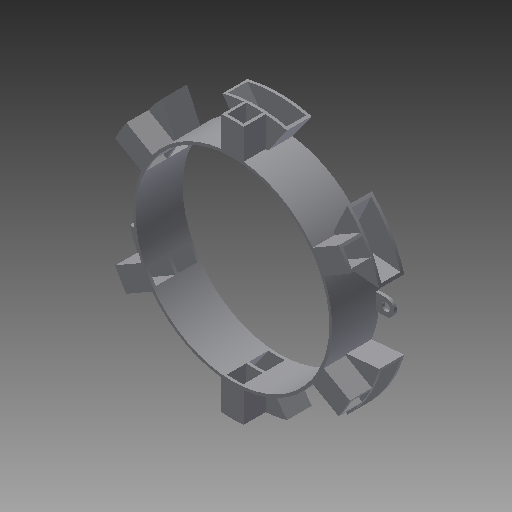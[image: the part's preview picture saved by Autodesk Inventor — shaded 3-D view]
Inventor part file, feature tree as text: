
AUTODESK INVENTOR PART (.ipt)
format: ipt  version: 2017 (Build 210142000, 142)  size: 384,000 bytes
history: native  units: mm
features: extrude x5, sketch x5, reference x4, plane x1
ambient origin geometry x8: Origin, YZ Plane, XZ Plane, XY Plane, X Axis, Y Axis, Z Axis, Center Point
bodies: Solid1 (feature_tree)
feature tree (15):
  extrude  "Extrusion1"  Depth=7.0mm TaperAngle=0.0deg
  extrude  "Extrusion2"  Depth=1.0mm TaperAngle=360.0deg
  sketch  "Sketch3"  dims[d31=7.0mm d32=0.0mm d35=1.0mm d36=0.0mm]
  extrude  "Extrusion4"  Depth=1.0mm TaperAngle=0.0deg
  extrude  "Extrusion5"  Depth=1.0mm
  plane  "Work Plane1"
  extrude  "Extrusion7"  [1 undecoded]
  sketch  "Sketch1"  dims[d10=60.0mm d12=360.0deg d15=7.0mm d16=0.0mm]
  sketch  "Sketch2"  dims[d18=1.0mm d19=0.0mm d27=60.0mm d29=360.0deg]
  sketch  "Sketch4"  dims[d60=1.0mm d61=0.0mm d62=1.0mm]
  sketch  "Sketch5"
  reference  "Reference7"
  reference  "Reference8"
  reference  "Reference9"
  reference  "Reference10"
note: 1 required parameter value undecoded (feature->parameter linkage not recoverable at this tier; creation-order binding heuristic only, values carry confidence <= 0.55)
